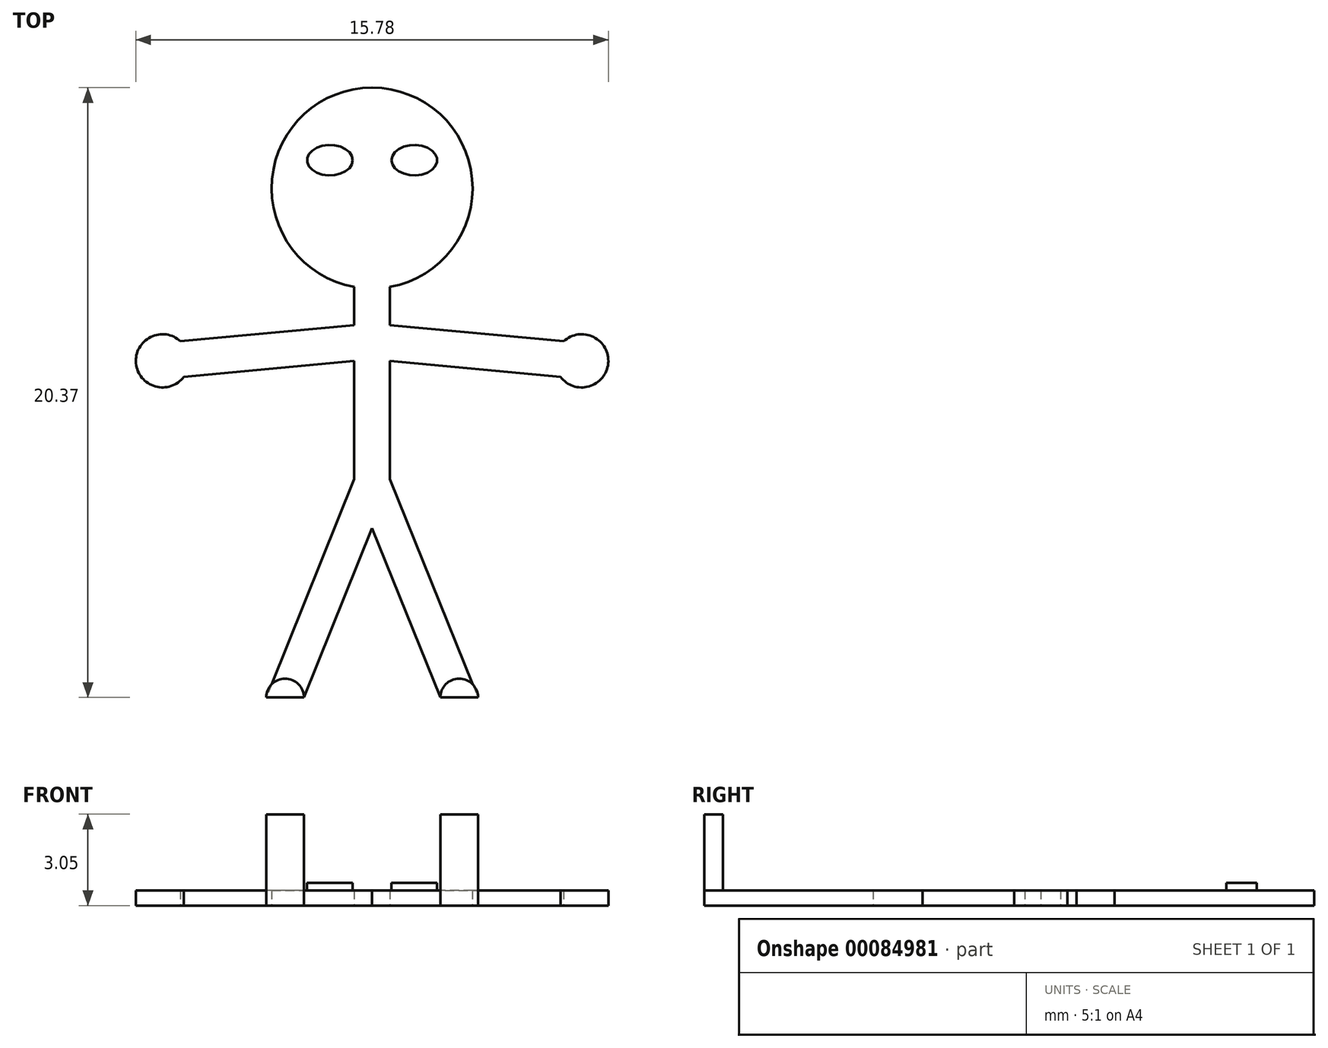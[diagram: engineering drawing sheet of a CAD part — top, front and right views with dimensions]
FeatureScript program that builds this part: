
annotation { "Feature Type Name" : "Feature", "Feature Type Description" : "" }
export const myFeature = defineFeature(function(context is Context, id is Id, definition is map)
    precondition{}
    {
        {
            var Q0;
            Q0=qCreatedBy(makeId("Top.planeOp"),FACE);
            var sketch = newSketch(context, id + "F0", { "sketchPlane" : qUnion([Q0])});
            skArc(sketch, "E0", {"start": v(0.6, 13.72) * mm, "mid": v(0, 20.37) * mm, "end": v(-0.6, 13.72) * mm});
            skLineSegment(sketch, "E1", {"start": v(-0.6, 13.72) * mm, "end": v(-0.6, 12.44) * mm});
            skLineSegment(sketch, "E2", {"start": v(-0.6, 12.44) * mm, "end": v(-7.06, 11.84) * mm});
            skLineSegment(sketch, "E3", {"start": v(-7.06, 11.84) * mm, "end": v(-6.95, 10.65) * mm});
            skLineSegment(sketch, "E4", {"start": v(-6.95, 10.65) * mm, "end": v(-0.6, 11.24) * mm});
            skLineSegment(sketch, "E5", {"start": v(-0.6, 11.24) * mm, "end": v(-0.6, 7.3) * mm});
            skLineSegment(sketch, "E6", {"start": v(-0.6, 7.3) * mm, "end": v(-3.54, 0) * mm});
            skLineSegment(sketch, "E7", {"start": v(-3.54, 0) * mm, "end": v(-2.28, 0) * mm});
            skLineSegment(sketch, "E8", {"start": v(-2.28, 0) * mm, "end": v(0, 5.65) * mm});
            skLineSegment(sketch, "E9.MirrorCS", {"start": v(0.6, 13.72) * mm, "end": v(0.6, 12.44) * mm});
            skLineSegment(sketch, "E10.MirrorCS", {"start": v(0.6, 12.44) * mm, "end": v(7.06, 11.84) * mm});
            skLineSegment(sketch, "E11.MirrorCS", {"start": v(6.95, 10.65) * mm, "end": v(0.6, 11.24) * mm});
            skLineSegment(sketch, "E12.MirrorCS", {"start": v(0.6, 11.24) * mm, "end": v(0.6, 7.3) * mm});
            skLineSegment(sketch, "E13.MirrorCS", {"start": v(0.6, 7.3) * mm, "end": v(3.54, 0) * mm});
            skLineSegment(sketch, "E14.MirrorCS", {"start": v(2.28, 0) * mm, "end": v(0, 5.65) * mm});
            skLineSegment(sketch, "E15.MirrorCS", {"start": v(7.06, 11.84) * mm, "end": v(6.95, 10.65) * mm});
            skLineSegment(sketch, "E16.MirrorCS", {"start": v(3.54, 0) * mm, "end": v(2.28, 0) * mm});
            skPoint(sketch, "E17.orphan", {"position": v(-0.6, 14.3) * mm});
            skPoint(sketch, "E18.orphan", {"position": v(0.6, 14.3) * mm});
            skPoint(sketch, "E19.MirrorCS.end.orphan", {"position": v(5.86, 11.84) * mm});
            skPoint(sketch, "E19.MirrorCS.start.orphan", {"position": v(-0.6, 12.44) * mm});
            skCircle(sketch, "E20", {"center": v(-7, 11.25) * mm, "radius": 0.89 * mm});
            skCircle(sketch, "E21.MirrorC", {"center": v(7, 11.25) * mm, "radius": 0.89 * mm});
            skSolve(sketch);
        }
        {
            var Q0;
            Q0 = qSketchRegion(id + "F0", true);
            extrude(context, id + "F1", {"entities" : qUnion([Q0]), "depth" : 0.5 * mm});
        }
        {
            var Q0;
            Q0=makeQuery(id+"F1.opExtrude","CAP_FACE",FACE,{"disambiguationData":[OSD([sQuery(id+"F0.wireOp",EDGE,"E0"),sQuery(id+"F0.wireOp",EDGE,"E1"),sQuery(id+"F0.wireOp",EDGE,"E2"),sQuery(id+"F0.wireOp",EDGE,"E4"),sQuery(id+"F0.wireOp",EDGE,"E5"),sQuery(id+"F0.wireOp",EDGE,"E6"),sQuery(id+"F0.wireOp",EDGE,"E7"),sQuery(id+"F0.wireOp",EDGE,"E8"),sQuery(id+"F0.wireOp",EDGE,"E9.MirrorCS"),sQuery(id+"F0.wireOp",EDGE,"E10.MirrorCS"),sQuery(id+"F0.wireOp",EDGE,"E11.MirrorCS"),sQuery(id+"F0.wireOp",EDGE,"E12.MirrorCS"),sQuery(id+"F0.wireOp",EDGE,"E13.MirrorCS"),sQuery(id+"F0.wireOp",EDGE,"E14.MirrorCS"),sQuery(id+"F0.wireOp",EDGE,"E16.MirrorCS"),sQuery(id+"F0.wireOp",EDGE,"E20"),sQuery(id+"F0.wireOp",EDGE,"E21.MirrorC")])],"isStart":false});
            var sketch = newSketch(context, id + "F2", { "sketchPlane" : qUnion([Q0])});
            skArc(sketch, "E22", {"start": v(-2.28, 0) * mm, "mid": v(-2.9, 0.63) * mm, "end": v(-3.54, 0) * mm});
            skLineSegment(sketch, "E23", {"start": v(-3.54, 0) * mm, "end": v(-2.28, 0) * mm});
            skArc(sketch, "E24.MirrorCS", {"start": v(2.28, 0) * mm, "mid": v(2.9, 0.63) * mm, "end": v(3.54, 0) * mm});
            skLineSegment(sketch, "E25.MirrorCS", {"start": v(3.54, 0) * mm, "end": v(2.28, 0) * mm});
            skSolve(sketch);
        }
        {
            var Q0;
            Q0 = qSketchRegion(id + "F2", true);
            extrude(context, id + "F3", {"entities" : qUnion([Q0]), "operationType" : NewBodyOperationType.ADD, "depth" : 2.54 * mm});
        }
        {
            var Q0;
            Q0=makeQuery(id+"F1.opExtrude","CAP_FACE",FACE,{"disambiguationData":[OSD([sQuery(id+"F0.wireOp",EDGE,"E0"),sQuery(id+"F0.wireOp",EDGE,"E1"),sQuery(id+"F0.wireOp",EDGE,"E2"),sQuery(id+"F0.wireOp",EDGE,"E4"),sQuery(id+"F0.wireOp",EDGE,"E5"),sQuery(id+"F0.wireOp",EDGE,"E6"),sQuery(id+"F0.wireOp",EDGE,"E7"),sQuery(id+"F0.wireOp",EDGE,"E8"),sQuery(id+"F0.wireOp",EDGE,"E9.MirrorCS"),sQuery(id+"F0.wireOp",EDGE,"E10.MirrorCS"),sQuery(id+"F0.wireOp",EDGE,"E11.MirrorCS"),sQuery(id+"F0.wireOp",EDGE,"E12.MirrorCS"),sQuery(id+"F0.wireOp",EDGE,"E13.MirrorCS"),sQuery(id+"F0.wireOp",EDGE,"E14.MirrorCS"),sQuery(id+"F0.wireOp",EDGE,"E16.MirrorCS"),sQuery(id+"F0.wireOp",EDGE,"E20"),sQuery(id+"F0.wireOp",EDGE,"E21.MirrorC")])],"isStart":false});
            var sketch = newSketch(context, id + "F4", { "sketchPlane" : qUnion([Q0])});
            skEllipse(sketch, "E26", {"center": v(-1.4, 17.95) * mm, "majorRadius": 0.76 * mm, "minorRadius": 0.5 * mm, "majorAxis": v(1, 0)});
            skEllipse(sketch, "E27.MirrorC", {"center": v(1.4, 17.95) * mm, "majorRadius": 0.76 * mm, "minorRadius": 0.5 * mm, "majorAxis": v(-1, 0)});
            skSolve(sketch);
        }
        {
            var Q0;
            Q0 = qSketchRegion(id + "F4", true);
            extrude(context, id + "F5", {"entities" : qUnion([Q0]), "operationType" : NewBodyOperationType.ADD, "depth" : 0.25 * mm});
        }
    });
